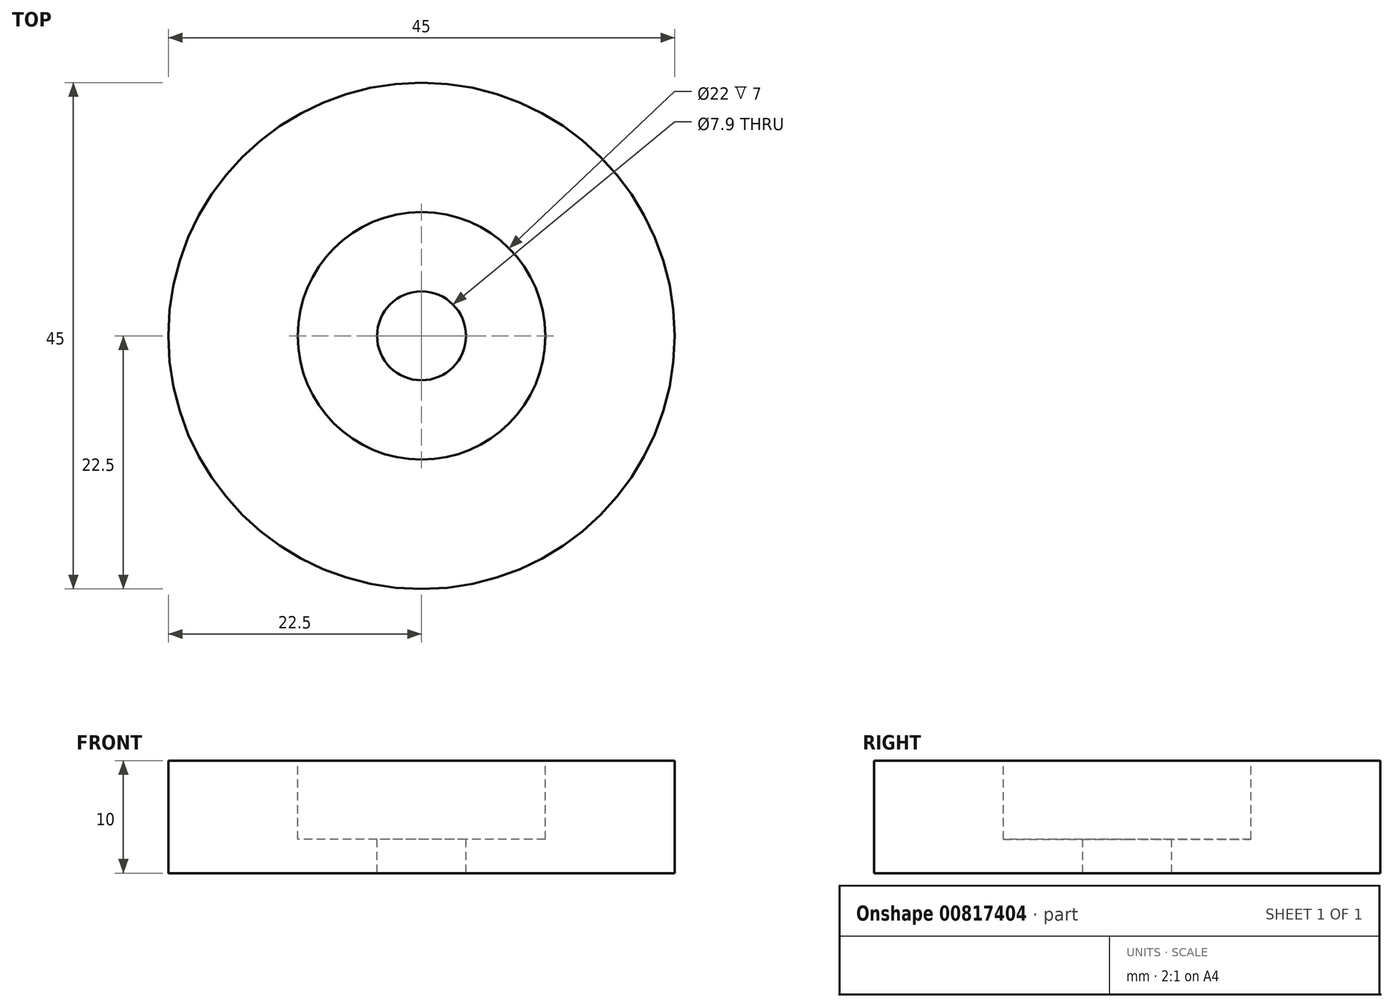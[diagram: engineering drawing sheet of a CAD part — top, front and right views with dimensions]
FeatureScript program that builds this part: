
annotation { "Feature Type Name" : "Feature", "Feature Type Description" : "" }
export const myFeature = defineFeature(function(context is Context, id is Id, definition is map)
    precondition{}
    {
        {
            var Q0;
            Q0=qCreatedBy(makeId("Top.planeOp"),FACE);
            var sketch = newSketch(context, id + "F0", { "sketchPlane" : qUnion([Q0])});
            skCircle(sketch, "E0", {"center": v(0, 0) * mm, "radius": 22.5 * mm});
            skSolve(sketch);
        }
        {
            var Q0;
            Q0=makeQuery(id+"F0.imprint","IMPRINT",FACE,{"disambiguationData":[TD([[makeQuery(id+"F0.imprint","IMPRINT",EDGE,{"derivedFrom":sQuery(id+"F0.wireOp",EDGE,"E0")}),1.0]])]});
            extrude(context, id + "F1", {"entities" : qUnion([Q0]), "depth" : 10 * mm, "offsetDistance" : 25 * mm});
        }
        {
            var Q0;
            Q0=makeQuery(id+"F1.opExtrude","CAP_FACE",FACE,{"disambiguationData":[OSD([sQuery(id+"F0.wireOp",EDGE,"E0")])],"isStart":false});
            var sketch = newSketch(context, id + "F2", { "sketchPlane" : qUnion([Q0])});
            skCircle(sketch, "E1", {"center": v(0, 0) * mm, "radius": 11 * mm});
            skSolve(sketch);
        }
        {
            var Q0;
            Q0=makeQuery(id+"F2.imprint","IMPRINT",FACE,{"disambiguationData":[TD([[makeQuery(id+"F2.imprint","IMPRINT",EDGE,{"derivedFrom":sQuery(id+"F2.wireOp",EDGE,"E1")}),1.0]])]});
            extrude(context, id + "F3", {"entities" : qUnion([Q0]), "operationType" : NewBodyOperationType.REMOVE, "oppositeDirection" : true, "depth" : 7 * mm, "offsetDistance" : 25 * mm});
        }
        {
            var Q0;
            Q0=makeQuery(id+"F3.boolean.opBoolean","COPY",FACE,{"derivedFrom":makeQuery(id+"F3.opExtrude","CAP_FACE",FACE,{"disambiguationData":[OSD([sQuery(id+"F2.wireOp",EDGE,"E1")])],"isStart":false})});
            var sketch = newSketch(context, id + "F4", { "sketchPlane" : qUnion([Q0])});
            skCircle(sketch, "E2", {"center": v(0, 0) * mm, "radius": 3.95 * mm});
            skSolve(sketch);
        }
        {
            var Q0;
            Q0=makeQuery(id+"F4.imprint","IMPRINT",FACE,{"disambiguationData":[TD([[makeQuery(id+"F4.imprint","IMPRINT",EDGE,{"derivedFrom":sQuery(id+"F4.wireOp",EDGE,"E2")}),1.0]])]});
            extrude(context, id + "F5", {"entities" : qUnion([Q0]), "operationType" : NewBodyOperationType.REMOVE, "oppositeDirection" : true, "depth" : 25 * mm, "offsetDistance" : 25 * mm});
        }
    });
